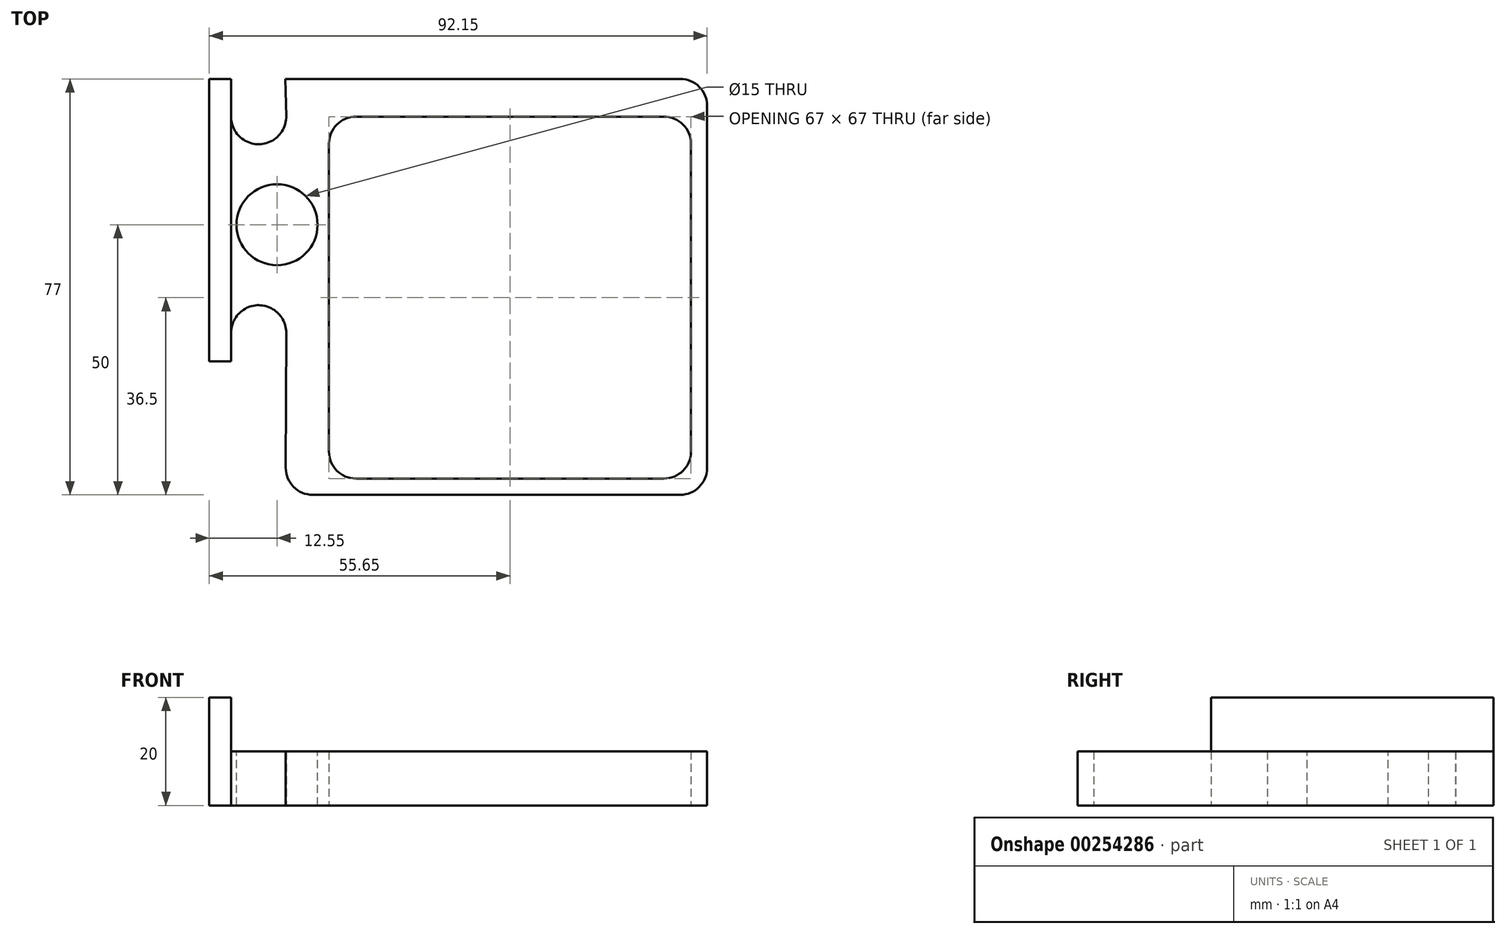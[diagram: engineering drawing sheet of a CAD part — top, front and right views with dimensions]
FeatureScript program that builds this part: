
annotation { "Feature Type Name" : "Feature", "Feature Type Description" : "" }
export const myFeature = defineFeature(function(context is Context, id is Id, definition is map)
    precondition{}
    {
        {
            var Q0;
            Q0=qCreatedBy(makeId("Top.planeOp"),FACE);
            var sketch = newSketch(context, id + "F0", { "sketchPlane" : qUnion([Q0])});
            skLineSegment(sketch, "E0", {"start": v(57.6, 15) * mm, "end": v(57.6, -42) * mm});
            skLineSegment(sketch, "E1", {"start": v(52.6, -47) * mm, "end": v(-4.4, -47) * mm});
            skLineSegment(sketch, "E2", {"start": v(-4.4, 20) * mm, "end": v(52.6, 20) * mm});
            skLineSegment(sketch, "E3", {"start": v(-15.4, -20) * mm, "end": v(-15.4, -45) * mm});
            skLineSegment(sketch, "E4.0", {"start": v(-9.4, 15) * mm, "end": v(-9.4, -42) * mm});
            skLineSegment(sketch, "E5.0", {"start": v(55.6, -50) * mm, "end": v(-12.4, -50) * mm});
            skLineSegment(sketch, "E6.0", {"start": v(60.6, 22) * mm, "end": v(60.6, -45) * mm});
            skLineSegment(sketch, "E7.0", {"start": v(-17.44, 27) * mm, "end": v(55.6, 27) * mm});
            skPoint(sketch, "E8.visualSharp", {"position": v(-9.4, 20) * mm});
            skArc(sketch, "E8.filletArc", {"start": v(-4.4, 20) * mm, "mid": v(-7.94, 18.54) * mm, "end": v(-9.4, 15) * mm});
            skPoint(sketch, "E9.visualSharp", {"position": v(57.6, 20) * mm});
            skArc(sketch, "E9.filletArc", {"start": v(57.6, 15) * mm, "mid": v(56.14, 18.54) * mm, "end": v(52.6, 20) * mm});
            skPoint(sketch, "E10.visualSharp", {"position": v(57.6, -47) * mm});
            skArc(sketch, "E10.filletArc", {"start": v(52.6, -47) * mm, "mid": v(56.14, -45.54) * mm, "end": v(57.6, -42) * mm});
            skPoint(sketch, "E11.visualSharp", {"position": v(-9.4, -47) * mm});
            skArc(sketch, "E11.filletArc", {"start": v(-9.4, -42) * mm, "mid": v(-7.94, -45.54) * mm, "end": v(-4.4, -47) * mm});
            skPoint(sketch, "E12.visualSharp", {"position": v(60.6, 27) * mm});
            skArc(sketch, "E12.filletArc", {"start": v(60.6, 22) * mm, "mid": v(59.14, 25.54) * mm, "end": v(55.6, 27) * mm});
            skPoint(sketch, "E13.visualSharp", {"position": v(60.6, -50) * mm});
            skArc(sketch, "E13.filletArc", {"start": v(55.6, -50) * mm, "mid": v(59.14, -48.54) * mm, "end": v(60.6, -45) * mm});
            skPoint(sketch, "E14.visualSharp", {"position": v(-15.4, -50) * mm});
            skPoint(sketch, "E15.visualSharp", {"position": v(-17.4, -50) * mm});
            skArc(sketch, "E15.filletArc", {"start": v(-17.4, -45) * mm, "mid": v(-15.93, -48.54) * mm, "end": v(-12.4, -50) * mm});
            skLineSegment(sketch, "E16", {"start": v(-17.3, 20.1) * mm, "end": v(-17.44, 27) * mm});
            skLineSegment(sketch, "E17", {"start": v(-27.5, 19.92) * mm, "end": v(-27.5, 27) * mm});
            skLineSegment(sketch, "E18", {"start": v(-31.55, 27) * mm, "end": v(-31.55, -25.3) * mm});
            skLineSegment(sketch, "E19", {"start": v(-31.55, 27) * mm, "end": v(-27.5, 27) * mm});
            skArc(sketch, "E20", {"start": v(-27.5, 19.92) * mm, "mid": v(-22.3, 14.9) * mm, "end": v(-17.3, 20.1) * mm});
            skLineSegment(sketch, "E21", {"start": v(-17.3, -20.06) * mm, "end": v(-17.4, -45) * mm});
            skArc(sketch, "E22", {"start": v(-17.3, -20.06) * mm, "mid": v(-22.36, -14.9) * mm, "end": v(-27.5, -19.99) * mm});
            skLineSegment(sketch, "E23", {"start": v(-27.5, -19.99) * mm, "end": v(-27.5, -25.3) * mm});
            skLineSegment(sketch, "E24", {"start": v(-27.5, -25.3) * mm, "end": v(-31.55, -25.3) * mm});
            skPoint(sketch, "E25.orphan", {"position": v(-31.55, -25.78) * mm});
            skSolve(sketch);
        }
        {
            var Q0;
            Q0=makeQuery(id+"F0.imprint","IMPRINT",FACE,{"disambiguationData":[TD([[makeQuery(id+"F0.imprint","IMPRINT",EDGE,{"derivedFrom":sQuery(id+"F0.wireOp",EDGE,"E0")}),1.0]])]});
            var Q1;
            {var subQ5=sQuery(id+"F0.wireOp",EDGE,"uBORmjYi-vxya-RGDX-7Kvu-OBbsLZReanTz");var subQ7=sQuery(id+"F0.wireOp",EDGE,"eZt0HCq9-thl3-nhVQ-AJAq-lgKIe9nYUzs1");var subQ8=makeQuery(id+"F0.imprint","INTERSECT",VERTEX,{"derivedFrom":[subQ7,subQ5]});Q1=makeQuery(id+"F0.imprint","IMPRINT",FACE,{"disambiguationData":[TD([[makeQuery(id+"F0.imprint","IMPRINT",EDGE,{"disambiguationData":[TD([[subQ8,1.0]])],"derivedFrom":subQ7}),-1.0]])]});}
            var Q2;
            {var subQ2=sQuery(id+"F0.wireOp",EDGE,"2d47d340-5632-42c6-b5a1-90fe0f84497d0.MirrorCS");var subQ7=sQuery(id+"F0.wireOp",EDGE,"f5KNxZPc-6qdK-B31N-WPcH-DImWyV9YgfT0");var subQ8=makeQuery(id+"F0.imprint","INTERSECT",VERTEX,{"derivedFrom":[subQ7,subQ2]});Q2=makeQuery(id+"F0.imprint","IMPRINT",FACE,{"disambiguationData":[TD([[makeQuery(id+"F0.imprint","IMPRINT",EDGE,{"disambiguationData":[TD([[subQ8,-1.0]])],"derivedFrom":subQ7}),-1.0]])]});}
            extrude(context, id + "F1", {"entities" : qUnion([Q0, Q1, Q2]), "depth" : 10 * mm});
        }
        {
            var Q0;
            Q0=makeQuery(id+"F1.opExtrude","CAP_FACE",FACE,{"disambiguationData":[OSD([sQuery(id+"F0.wireOp",EDGE,"E0"),sQuery(id+"F0.wireOp",EDGE,"E1"),sQuery(id+"F0.wireOp",EDGE,"E2"),sQuery(id+"F0.wireOp",EDGE,"E4.0"),sQuery(id+"F0.wireOp",EDGE,"E5.0"),sQuery(id+"F0.wireOp",EDGE,"E6.0"),sQuery(id+"F0.wireOp",EDGE,"E7.0"),sQuery(id+"F0.wireOp",EDGE,"E8.filletArc"),sQuery(id+"F0.wireOp",EDGE,"E9.filletArc"),sQuery(id+"F0.wireOp",EDGE,"E10.filletArc"),sQuery(id+"F0.wireOp",EDGE,"E11.filletArc"),sQuery(id+"F0.wireOp",EDGE,"E12.filletArc"),sQuery(id+"F0.wireOp",EDGE,"E13.filletArc"),sQuery(id+"F0.wireOp",EDGE,"E15.filletArc"),sQuery(id+"F0.wireOp",EDGE,"E16"),sQuery(id+"F0.wireOp",EDGE,"E17"),sQuery(id+"F0.wireOp",EDGE,"E18"),sQuery(id+"F0.wireOp",EDGE,"E19"),sQuery(id+"F0.wireOp",EDGE,"E20"),sQuery(id+"F0.wireOp",EDGE,"E21"),sQuery(id+"F0.wireOp",EDGE,"E22"),sQuery(id+"F0.wireOp",EDGE,"E23"),sQuery(id+"F0.wireOp",EDGE,"E24")])],"isStart":false});
            var sketch = newSketch(context, id + "F2", { "sketchPlane" : qUnion([Q0])});
            skCircle(sketch, "E26", {"center": v(-19, 0) * mm, "radius": 7.5 * mm});
            skLineSegment(sketch, "E27", {"start": v(-31.55, 27) * mm, "end": v(-31.55, -25.3) * mm});
            skLineSegment(sketch, "E28", {"start": v(-31.55, -25.3) * mm, "end": v(-27.5, -25.3) * mm});
            skLineSegment(sketch, "E29", {"start": v(-27.5, -25.3) * mm, "end": v(-27.5, 27) * mm});
            skLineSegment(sketch, "E30", {"start": v(-27.5, 27) * mm, "end": v(-31.55, 27) * mm});
            skSolve(sketch);
        }
        {
            var Q0;
            Q0=makeQuery(id+"F2.imprint","IMPRINT",FACE,{"disambiguationData":[TD([[makeQuery(id+"F2.imprint","IMPRINT",EDGE,{"derivedFrom":sQuery(id+"F2.wireOp",EDGE,"E27")}),1.0]])]});
            extrude(context, id + "F3", {"entities" : qUnion([Q0]), "operationType" : NewBodyOperationType.ADD, "depth" : 10 * mm});
        }
        {
            var Q0;
            Q0=makeQuery(id+"F2.imprint","IMPRINT",FACE,{"disambiguationData":[TD([[makeQuery(id+"F2.imprint","IMPRINT",EDGE,{"derivedFrom":sQuery(id+"F2.wireOp",EDGE,"E26")}),1.0]])]});
            extrude(context, id + "F4", {"entities" : qUnion([Q0]), "operationType" : NewBodyOperationType.REMOVE, "oppositeDirection" : true, "depth" : 25 * mm});
        }
    });
